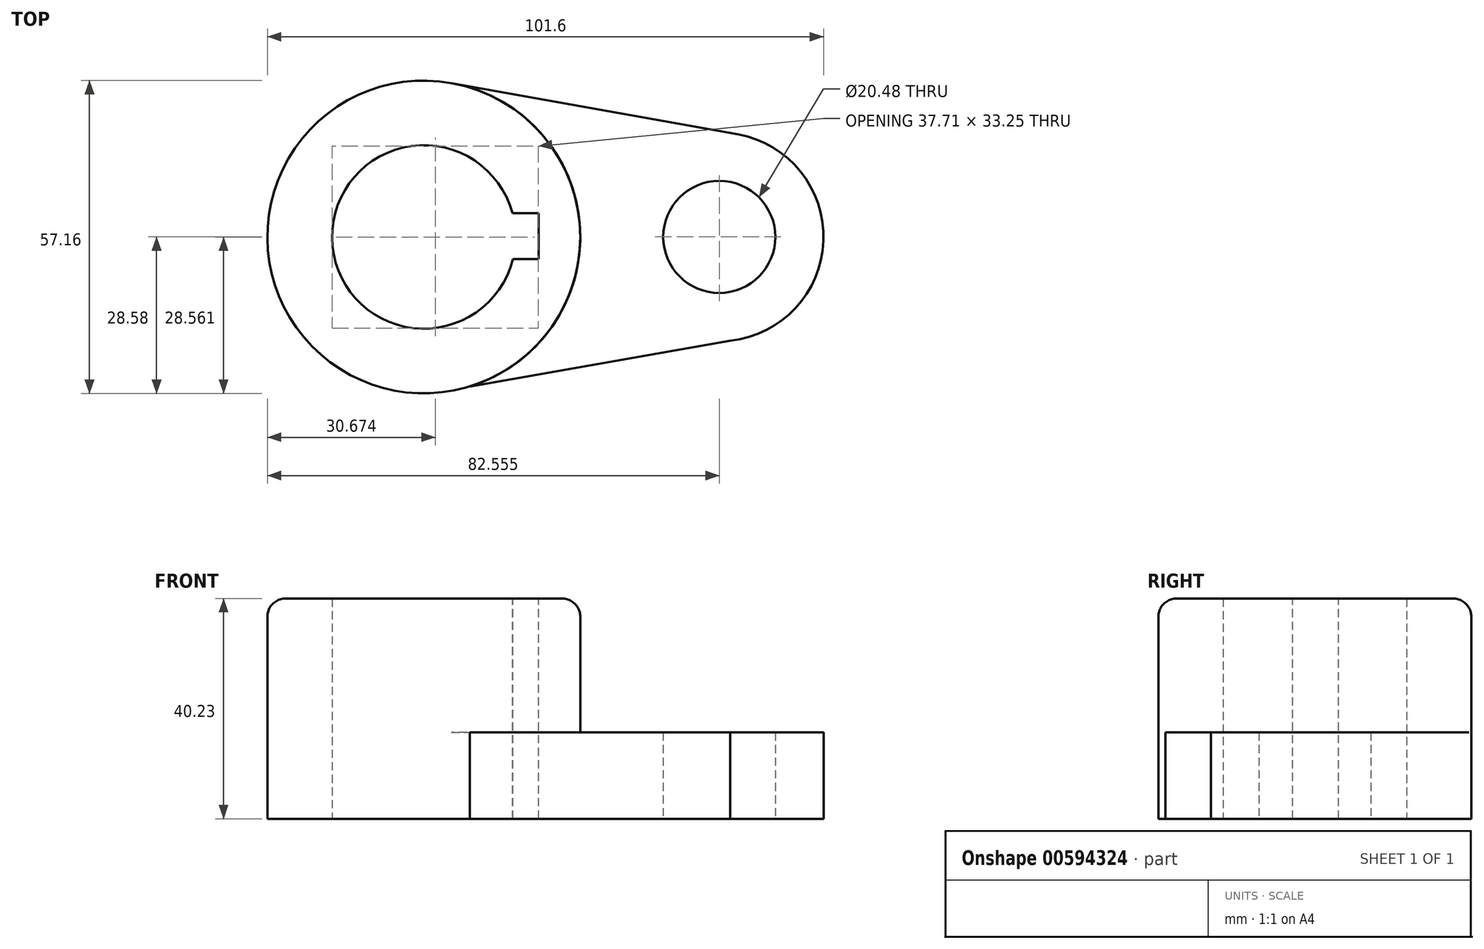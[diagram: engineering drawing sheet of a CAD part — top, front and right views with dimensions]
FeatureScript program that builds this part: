
annotation { "Feature Type Name" : "Feature", "Feature Type Description" : "" }
export const myFeature = defineFeature(function(context is Context, id is Id, definition is map)
    precondition{}
    {
        {
            var Q0;
            Q0=qCreatedBy(makeId("Top.planeOp"),FACE);
            var sketch = newSketch(context, id + "F0", { "sketchPlane" : qUnion([Q0])});
            skCircle(sketch, "E0", {"center": v(0, 0) * mm, "radius": 28.58 * mm});
            skArc(sketch, "E1", {"start": v(55.97, -18.95) * mm, "mid": v(73.01, -0.69) * mm, "end": v(57.34, 18.75) * mm});
            skLineSegment(sketch, "E2", {"start": v(5.04, 28.13) * mm, "end": v(57.34, 18.75) * mm});
            skLineSegment(sketch, "E3", {"start": v(58.56, -18.49) * mm, "end": v(8.4, -27.31) * mm});
            skCircle(sketch, "E4", {"center": v(53.98, 0) * mm, "radius": 10.24 * mm});
            skCircle(sketch, "E5", {"center": v(0, 0) * mm, "radius": 16.76 * mm});
            skSolve(sketch);
        }
        {
            var Q0;
            Q0 = qSketchRegion(id + "F0", true);
            extrude(context, id + "F1", {"entities" : qUnion([Q0]), "depth" : 15.77 * mm, "offsetDistance" : 25.4 * mm});
        }
        {
            var Q0;
            Q0=makeQuery(id+"F0.imprint","IMPRINT",FACE,{"disambiguationData":[TD([[makeQuery(id+"F0.imprint","IMPRINT",EDGE,{"derivedFrom":sQuery(id+"F0.wireOp",EDGE,"E5")}),-1.0]])]});
            extrude(context, id + "F2", {"entities" : qUnion([Q0]), "operationType" : NewBodyOperationType.ADD, "depth" : 40.23 * mm, "offsetDistance" : 25.4 * mm});
        }
        {
            var Q0;
            Q0=makeQuery(id+"F2.opExtrude","CAP_FACE",FACE,{"disambiguationData":[OSD([sQuery(id+"F0.wireOp",EDGE,"E0"),sQuery(id+"F0.wireOp",EDGE,"E5")])],"isStart":false});
            var sketch = newSketch(context, id + "F3", { "sketchPlane" : qUnion([Q0])});
            skLineSegment(sketch, "E6.bottom", {"start": v(16.19, 4.36) * mm, "end": v(20.95, 4.36) * mm});
            skLineSegment(sketch, "E6.top", {"start": v(16.19, -4.06) * mm, "end": v(20.95, -4.06) * mm});
            skLineSegment(sketch, "E6.left", {"start": v(16.19, 4.36) * mm, "end": v(16.19, -4.06) * mm});
            skLineSegment(sketch, "E6.right", {"start": v(20.95, 4.36) * mm, "end": v(20.95, -4.06) * mm});
            skSolve(sketch);
        }
        {
            var Q0;
            {var subQ0=sQuery(id+"F3.wireOp",EDGE,"E6.bottom");Q0=makeQuery(id+"F3.imprint","IMPRINT",FACE,{"disambiguationData":[TD([[makeQuery(id+"F3.imprint","IMPRINT",EDGE,{"derivedFrom":subQ0}),-1.0]])]});}
            extrude(context, id + "F4", {"entities" : qUnion([Q0]), "operationType" : NewBodyOperationType.REMOVE, "oppositeDirection" : true, "depth" : 57.9 * mm, "offsetDistance" : 25.4 * mm});
        }
        {
            var Q0;
            Q0=makeQuery(id+"F2.opExtrude","CAP_EDGE",EDGE,{"disambiguationData":[OSD([sQuery(id+"F0.wireOp",EDGE,"E0")])],"isStart":false});
            fillet(context, id + "F5", {"entities" : qUnion([Q0]), "radius" : 3.3 * mm, "tangentPropagation" : true, "allowEdgeOverflow" : false});
        }
    });
